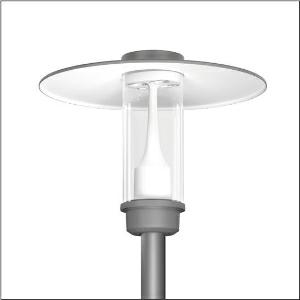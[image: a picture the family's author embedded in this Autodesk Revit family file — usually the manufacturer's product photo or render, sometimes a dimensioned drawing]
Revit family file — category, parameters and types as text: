
# Revit family: litepole_2_iq___p1_0a_5xa5425nf14h_2791
name_source: partatom
category: Lighting Fixtures
units: mm (PartAtom-declared; Revit-internal decimal feet)

## family parameters
Cut with Voids When Loaded = No
Host = Face
Light Source = No
Part Type = Normal
Room Calculation Point = No
Round Connector Dimension = Use Diameter
Shared = No

## types (1)
- --- (1 x LED, 1520 lm, 11.8 W, 2700K)
    Apparent Load = 12 VA
    CIE Flux Codes = 33 62 89 96 100
    Color Rendering = 70
    Color Temperature = 2700K
    Default Elevation = 1800 mm
    Description = Litepole 2 iQ, mast luminaire, Module 540 iQ-SR, primary light control with 3 zone facetted reflector, of plastic, silver coated, highly specular, structured, primary optical cover: cover, of PMMA, transparent, light distribution: P1.0a, light emission: direct distribution, primary light characteristic: strongly asymmetric, installation type: post-top, LED, High Power LED, rated luminous flux: 1.520lm, luminous efficacy: 129lm/W, light colour: 727, colour temperature: 2700K, control gear: iQ Street-Remote, control: pre-setting: logarithmic dimming characteristic, Street-Remote, Auto-Match, Temp-Guard, Lumen-Switch, Night-Set, Smart-Wire, Light-Fading, Desk-Remote (wireless, voltage-free reading and setting of iQ features in the workshop via application-optimized NFC function/RFID function), optimised constant luminous flux control (CLO 2.0), with terminal, 6-pole, max. 2.5mm², mains connection: 230..240V, AC, 50/60Hz, start of lifetime: 12W, end of service life: 12W, reduction: 6W, luminaire housing, upper part, of aluminium, coated, Siteco® metallic grey (DB 702S), diameter: 750mm, height: 590mm, spigot size: d x l = 76 x 70mm (post-top) | with reducer (optional accessory) 60 x 70mm, mounting height: 3..5m, post-top mast mounting element, of diecast aluminium, coated, Siteco® metallic grey (DB 702S), Module 540 iQ-SR, traffic white (RAL 9016), equipment: standard, protection rating (complete): IP65, insulation class (complete): insulation class II (safety insulation), certification: CE, ENEC, VDE, packaging unit: 1 piece

Light Distribution: P1.0a
    Height = 590 mm
    Lamp = 1 x LED
    Lamp Light Flux = 1520 lm
    Lamp Power = 11.8 W
    Lamp count = 1
    Length = 750 mm
    Luminous efficacy = 129 lm/W
    Manufacturer = Siteco
    ModVariant = No
    Model = 5XA5425NF14H
    Number of Poles = 1
    OnlyDefault = Yes
    Power Factor = 1
    Product Name = Litepole 2 iQ | P1.0a
    Product group = mast luminaire | pylon top
    ProductGroupID = 6100
    Protection Class = Protection class II
    Protection Degree = IP 65
    RLX_Detail_Level = 1
    RLX_Emergency_Light_Flux = 0 lm
    RLX_Emergency_Type = 0
    RLX_Emergency_Type_DB = No
    RlxData = <blob elided: 55257 chars, md5=1c5efc09>
    Socket = socket
    Standby Power = 0 W
    System Light Flux = 1520 lm
    System Power = 12 W
    Type Comments = factory setting: luminous flux: 100 % | dim-lin: 254 | 472 mA
    Type Image = l_1006518.jpg
    URL = http://relux.com
    VarID = @adj_155675
    Voltage = 0 V
    Weight = 0.00 kg
    Width = 0 mm  [stored 0 ft]

note: [stored X ft] marks values corroborated as IEEE doubles in the binary element streams (Revit-internal decimal feet)

## geometry (parser evidence)
native form markers: Blend x4, Sweep x11
no freeform markers — native parametric forms only
